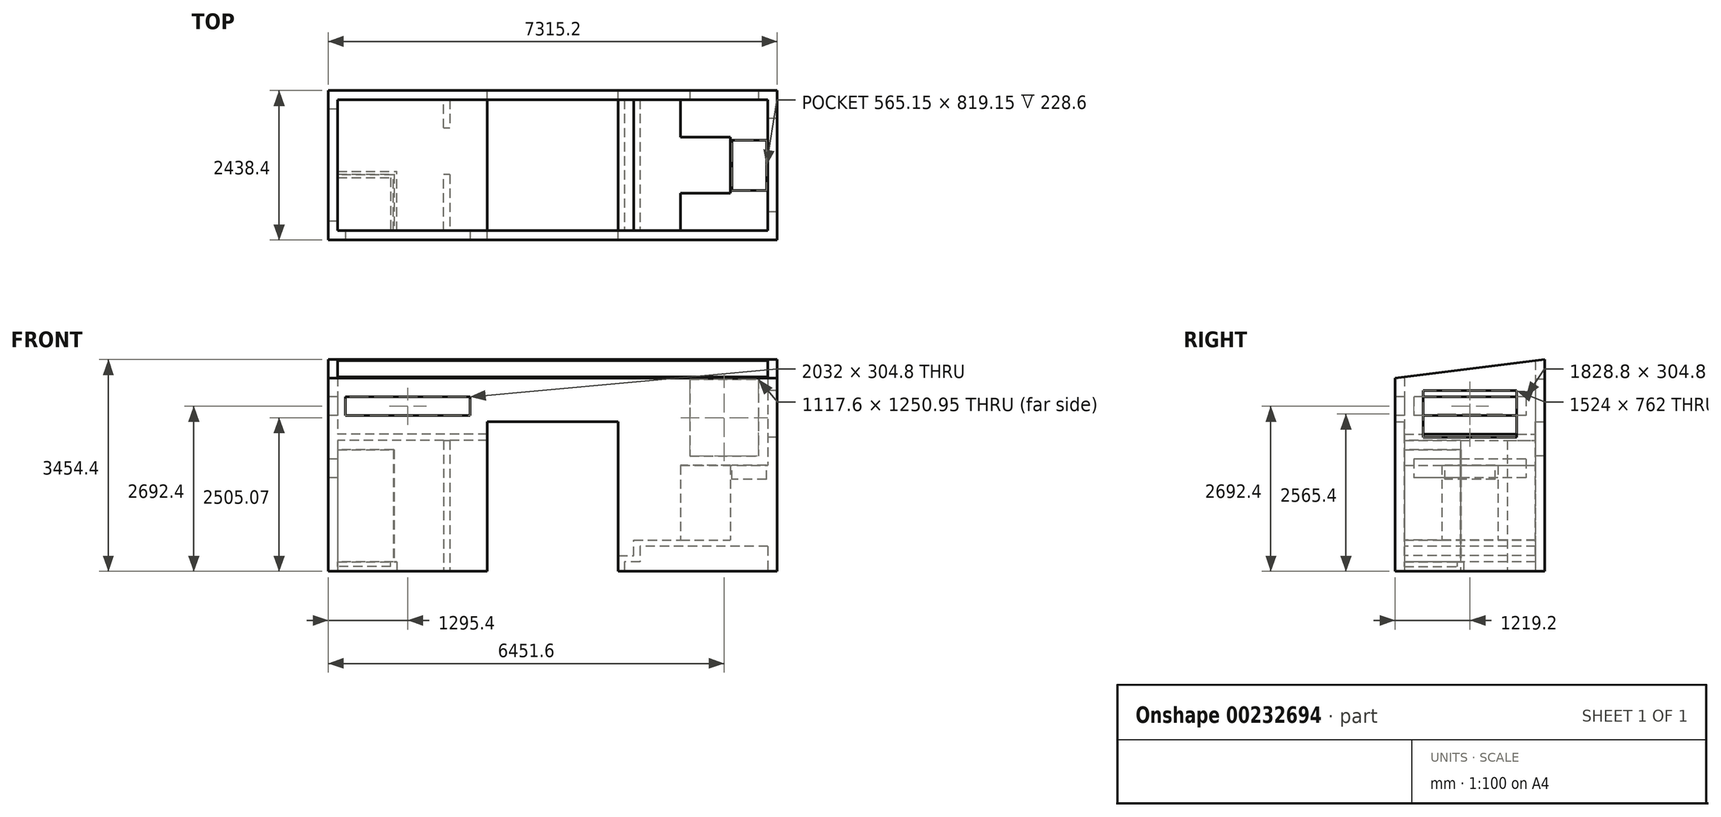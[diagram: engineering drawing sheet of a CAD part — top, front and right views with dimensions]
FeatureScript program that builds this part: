
annotation { "Feature Type Name" : "Feature", "Feature Type Description" : "" }
export const myFeature = defineFeature(function(context is Context, id is Id, definition is map)
    precondition{}
    {
        {
            var Q0;
            Q0=qCreatedBy(makeId("Top.planeOp"),FACE);
            var sketch = newSketch(context, id + "F0", { "sketchPlane" : qUnion([Q0])});
            skLineSegment(sketch, "E0.bottom", {"start": v(-3657.6, 1219.2) * mm, "end": v(3657.6, 1219.2) * mm});
            skLineSegment(sketch, "E0.top", {"start": v(-3657.6, -1219.2) * mm, "end": v(3657.6, -1219.2) * mm});
            skLineSegment(sketch, "E0.left", {"start": v(-3657.6, 1219.2) * mm, "end": v(-3657.6, -1219.2) * mm});
            skLineSegment(sketch, "E0.right", {"start": v(3657.6, 1219.2) * mm, "end": v(3657.6, -1219.2) * mm});
            skLineSegment(sketch, "E1", {"start": v(3657.6, 0) * mm, "end": v(-3657.6, 0) * mm, "construction": true});
            skLineSegment(sketch, "E2", {"start": v(0, 1219.2) * mm, "end": v(0, -1219.2) * mm, "construction": true});
            skSolve(sketch);
        }
        {
            var Q0;
            Q0 = qSketchRegion(id + "F0", true);
            extrude(context, id + "F1", {"entities" : qUnion([Q0]), "depth" : 4114.8 * mm - 660.4 * mm});
        }
        {
            var Q0;
            Q0=makeQuery(id+"F1.opExtrude","CAP_FACE",FACE,{"disambiguationData":[OSD([sQuery(id+"F0.wireOp",EDGE,"E0.bottom"),sQuery(id+"F0.wireOp",EDGE,"E0.top"),sQuery(id+"F0.wireOp",EDGE,"E0.left"),sQuery(id+"F0.wireOp",EDGE,"E0.right")])],"isStart":false});
            shell(context, id + "F2", {"entities" : qUnion([Q0]), "thickness" : 152.4 * mm});
        }
        {
            var Q0;
            Q0=makeQuery(id+"F1.opExtrude","SWEPT_FACE",FACE,{"disambiguationData":[OSD([sQuery(id+"F0.wireOp",EDGE,"E0.left")])]});
            var sketch = newSketch(context, id + "F3", { "sketchPlane" : qUnion([Q0])});
            skLineSegment(sketch, "E3", {"start": v(-1219.2, 3454.4) * mm, "end": v(1219.2, 3149.6) * mm});
            skLineSegment(sketch, "E4", {"start": v(1219.2, 3149.6) * mm, "end": v(1219.2, 3454.4) * mm});
            skLineSegment(sketch, "E5", {"start": v(1219.2, 3454.4) * mm, "end": v(-1219.2, 3454.4) * mm});
            skSolve(sketch);
        }
        {
            var Q0;
            Q0 = qSketchRegion(id + "F3", true);
            var Q1;
            Q1=makeQuery(id+"F1.opExtrude","SWEPT_FACE",FACE,{"disambiguationData":[OSD([sQuery(id+"F0.wireOp",EDGE,"E0.right")])]});
            extrude(context, id + "F4", {"entities" : qUnion([Q0]), "operationType" : NewBodyOperationType.REMOVE, "endBound" : BoundingType.UP_TO_SURFACE, "oppositeDirection" : true, "endBoundEntityFace" : qUnion([Q1]), "depth" : 25.4 * mm});
        }
        {
            var Q0;
            Q0=makeQuery(id+"F1.opExtrude","SWEPT_FACE",FACE,{"disambiguationData":[OSD([sQuery(id+"F0.wireOp",EDGE,"E0.bottom")])]});
            var sketch = newSketch(context, id + "F5", { "sketchPlane" : qUnion([Q0])});
            skLineSegment(sketch, "E6.bottom", {"start": v(-1066.8, 0) * mm, "end": v(1066.8, 0) * mm});
            skLineSegment(sketch, "E6.top", {"start": v(-1066.8, 2438.4) * mm, "end": v(1066.8, 2438.4) * mm});
            skLineSegment(sketch, "E6.left", {"start": v(-1066.8, 0) * mm, "end": v(-1066.8, 2438.4) * mm});
            skLineSegment(sketch, "E6.right", {"start": v(1066.8, 0) * mm, "end": v(1066.8, 2438.4) * mm});
            skLineSegment(sketch, "E7", {"start": v(0, 3454.4) * mm, "end": v(0, 0) * mm, "construction": true});
            skSolve(sketch);
        }
        {
            var Q0;
            Q0 = qSketchRegion(id + "F5", true);
            var Q1;
            Q1=makeQuery(id+"F1.opExtrude","SWEPT_FACE",FACE,{"disambiguationData":[OSD([sQuery(id+"F0.wireOp",EDGE,"E0.top")])]});
            extrude(context, id + "F6", {"entities" : qUnion([Q0]), "operationType" : NewBodyOperationType.REMOVE, "endBound" : BoundingType.UP_TO_SURFACE, "oppositeDirection" : true, "endBoundEntityFace" : qUnion([Q1]), "depth" : 25.4 * mm});
        }
        {
            var Q0;
            {var subQ0=sQuery(id+"F0.wireOp",EDGE,"E0.bottom");var subQ1=sQuery(id+"F0.wireOp",EDGE,"E0.top");var subQ2=sQuery(id+"F0.wireOp",EDGE,"E0.left");Q0=makeQuery(id+"F6.boolean.opBoolean","SPLIT",FACE,{"disambiguationData":[TD([makeQuery(id+"F2.opShell","OFFSET_FACE",FACE,{"disambiguationData":[OSD([subQ2])]})])],"derivedFrom":makeQuery(id+"F2.opShell","OFFSET_FACE",FACE,{"disambiguationData":[OSD([subQ0,subQ1,subQ2,sQuery(id+"F0.wireOp",EDGE,"E0.right")])]})});}
            var sketch = newSketch(context, id + "F7", { "sketchPlane" : qUnion([Q0])});
            skLineSegment(sketch, "E8.bottom", {"start": v(-3505.2, 1066.8) * mm, "end": v(3505.2, 1066.8) * mm});
            skLineSegment(sketch, "E8.top", {"start": v(-3505.2, -1066.8) * mm, "end": v(3505.2, -1066.8) * mm});
            skLineSegment(sketch, "E8.left", {"start": v(-3505.2, 1066.8) * mm, "end": v(-3505.2, -1066.8) * mm});
            skLineSegment(sketch, "E8.right", {"start": v(3505.2, 1066.8) * mm, "end": v(3505.2, -1066.8) * mm});
            skSolve(sketch);
        }
        {
            var Q0;
            Q0 = qSketchRegion(id + "F7", true);
            var Q1;
            {var subQ0=sQuery(id+"F0.wireOp",EDGE,"E0.bottom");var subQ1=sQuery(id+"F0.wireOp",EDGE,"E0.top");var subQ2=sQuery(id+"F0.wireOp",EDGE,"E0.left");Q1=makeQuery(id+"F6.boolean.opBoolean","SPLIT",FACE,{"disambiguationData":[TD([makeQuery(id+"F1.opExtrude","SWEPT_FACE",FACE,{"disambiguationData":[OSD([subQ2])]})])],"derivedFrom":makeQuery(id+"F1.opExtrude","CAP_FACE",FACE,{"disambiguationData":[OSD([subQ0,subQ1,subQ2,sQuery(id+"F0.wireOp",EDGE,"E0.right")])],"isStart":true})});}
            extrude(context, id + "F8", {"entities" : qUnion([Q0]), "operationType" : NewBodyOperationType.REMOVE, "endBound" : BoundingType.UP_TO_SURFACE, "oppositeDirection" : true, "endBoundEntityFace" : qUnion([Q1]), "depth" : 25.4 * mm});
        }
        {
            var Q0;
            Q0=makeQuery(id+"F8.boolean.opBoolean","MERGE",FACE,{"derivedFrom":[makeQuery(id+"F2.opShell","OFFSET_FACE",FACE,{"disambiguationData":[OSD([sQuery(id+"F0.wireOp",EDGE,"E0.left")])]}),makeQuery(id+"F8.opExtrude","SWEPT_FACE",FACE,{"disambiguationData":[OSD([sQuery(id+"F7.wireOp",EDGE,"E8.left")])]})]});
            var sketch = newSketch(context, id + "F9", { "sketchPlane" : qUnion([Q0])});
            skLineSegment(sketch, "E9.bottom", {"start": v(-1066.8, 2235.2) * mm, "end": v(1066.8, 2235.2) * mm});
            skLineSegment(sketch, "E9.top", {"start": v(-1066.8, 2133.6) * mm, "end": v(1066.8, 2133.6) * mm});
            skLineSegment(sketch, "E9.left", {"start": v(-1066.8, 2235.2) * mm, "end": v(-1066.8, 2133.6) * mm});
            skLineSegment(sketch, "E9.right", {"start": v(1066.8, 2235.2) * mm, "end": v(1066.8, 2133.6) * mm});
            skSolve(sketch);
        }
        {
            var Q0;
            Q0 = qSketchRegion(id + "F9", true);
            extrude(context, id + "F10", {"entities" : qUnion([Q0]), "operationType" : NewBodyOperationType.ADD, "depth" : 2438.4 * mm});
        }
        {
            var Q0;
            {var subQ0=sQuery(id+"F0.wireOp",EDGE,"E0.top");var subQ1=makeQuery(id+"F2.opShell","OFFSET_FACE",FACE,{"disambiguationData":[OSD([subQ0])]});var subQ4=sQuery(id+"F0.wireOp",EDGE,"E0.right");Q0=makeQuery(id+"F10.boolean.opBoolean","SPLIT",FACE,{"disambiguationData":[TD([makeQuery(id+"F2.opShell","OFFSET_FACE",FACE,{"disambiguationData":[OSD([subQ4])]})])],"derivedFrom":makeQuery(id+"F8.boolean.opBoolean","MERGE",FACE,{"derivedFrom":[subQ1,makeQuery(id+"F8.opExtrude","SWEPT_FACE",FACE,{"disambiguationData":[OSD([sQuery(id+"F7.wireOp",EDGE,"E8.top")])]})]})});}
            var sketch = newSketch(context, id + "F11", { "sketchPlane" : qUnion([Q0])});
            skLineSegment(sketch, "E10", {"start": v(-1066.8, 0) * mm, "end": v(-1066.8, 254) * mm});
            skLineSegment(sketch, "E11", {"start": v(-1066.8, 254) * mm, "end": v(-1320.8, 254) * mm});
            skLineSegment(sketch, "E12", {"start": v(-1320.8, 254) * mm, "end": v(-1320.8, 508) * mm});
            skLineSegment(sketch, "E13", {"start": v(-1320.8, 508) * mm, "end": v(-3657.6, 508) * mm});
            skLineSegment(sketch, "E14", {"start": v(-3657.6, 508) * mm, "end": v(-3657.6, 406.4) * mm});
            skLineSegment(sketch, "E15", {"start": v(-3657.6, 406.4) * mm, "end": v(-1422.4, 406.4) * mm});
            skLineSegment(sketch, "E16", {"start": v(-1422.4, 406.4) * mm, "end": v(-1422.4, 152.4) * mm});
            skLineSegment(sketch, "E17", {"start": v(-1422.4, 152.4) * mm, "end": v(-1168.4, 152.4) * mm});
            skLineSegment(sketch, "E18", {"start": v(-1168.4, 152.4) * mm, "end": v(-1168.4, 0) * mm});
            skLineSegment(sketch, "E19", {"start": v(-1168.4, 0) * mm, "end": v(-1066.8, 0) * mm});
            skSolve(sketch);
        }
        {
            var Q0;
            Q0 = qSketchRegion(id + "F11", true);
            var Q1;
            {var subQ1=sQuery(id+"F0.wireOp",EDGE,"E0.right");var subQ2=sQuery(id+"F0.wireOp",EDGE,"E0.bottom");var subQ3=makeQuery(id+"F2.opShell","OFFSET_FACE",FACE,{"disambiguationData":[OSD([subQ2])]});Q1=makeQuery(id+"F10.boolean.opBoolean","SPLIT",FACE,{"disambiguationData":[TD([makeQuery(id+"F2.opShell","OFFSET_FACE",FACE,{"disambiguationData":[OSD([subQ1])]})])],"derivedFrom":makeQuery(id+"F8.boolean.opBoolean","MERGE",FACE,{"derivedFrom":[subQ3,makeQuery(id+"F8.opExtrude","SWEPT_FACE",FACE,{"disambiguationData":[OSD([sQuery(id+"F7.wireOp",EDGE,"E8.bottom")])]})]})});}
            extrude(context, id + "F12", {"entities" : qUnion([Q0]), "operationType" : NewBodyOperationType.ADD, "endBound" : BoundingType.UP_TO_SURFACE, "endBoundEntityFace" : qUnion([Q1]), "depth" : 25.4 * mm});
        }
        {
            var Q0;
            {var subQ4=sQuery(id+"F0.wireOp",EDGE,"E0.right");var subQ5=makeQuery(id+"F2.opShell","OFFSET_FACE",FACE,{"disambiguationData":[OSD([subQ4])]});var subQ6=sQuery(id+"F0.wireOp",EDGE,"E0.left");var subQ7=makeQuery(id+"F2.opShell","OFFSET_FACE",FACE,{"disambiguationData":[OSD([subQ6])]});var subQ10=sQuery(id+"F0.wireOp",EDGE,"E0.bottom");var subQ11=makeQuery(id+"F2.opShell","OFFSET_FACE",FACE,{"disambiguationData":[OSD([subQ10])]});Q0=makeQuery(id+"F12.boolean.opBoolean","SPLIT",FACE,{"disambiguationData":[TD([subQ7])],"derivedFrom":makeQuery(id+"F10.boolean.opBoolean","SPLIT",FACE,{"disambiguationData":[TD([subQ5])],"derivedFrom":makeQuery(id+"F8.boolean.opBoolean","MERGE",FACE,{"derivedFrom":[subQ11,makeQuery(id+"F8.opExtrude","SWEPT_FACE",FACE,{"disambiguationData":[OSD([sQuery(id+"F7.wireOp",EDGE,"E8.bottom")])]})]})})});}
            var sketch = newSketch(context, id + "F13", { "sketchPlane" : qUnion([Q0])});
            skLineSegment(sketch, "E20.bottom", {"start": v(2235.2, 3130.55) * mm, "end": v(3352.8, 3130.55) * mm});
            skLineSegment(sketch, "E20.top", {"start": v(2235.2, 1879.6) * mm, "end": v(3352.8, 1879.6) * mm});
            skLineSegment(sketch, "E20.left", {"start": v(2235.2, 3130.55) * mm, "end": v(2235.2, 1879.6) * mm});
            skLineSegment(sketch, "E20.right", {"start": v(3352.8, 3130.55) * mm, "end": v(3352.8, 1879.6) * mm});
            skSolve(sketch);
        }
        {
            var Q0;
            Q0=makeQuery(id+"F13.imprint","IMPRINT",FACE,{"disambiguationData":[TD([[makeQuery(id+"F13.imprint","IMPRINT",EDGE,{"derivedFrom":sQuery(id+"F13.wireOp",EDGE,"E20.bottom")}),-1.0]])]});
            var Q1;
            Q1=makeQuery(id+"F1.opExtrude","SWEPT_FACE",FACE,{"disambiguationData":[OSD([sQuery(id+"F0.wireOp",EDGE,"E0.bottom")])]});
            extrude(context, id + "F14", {"entities" : qUnion([Q0]), "operationType" : NewBodyOperationType.REMOVE, "endBound" : BoundingType.UP_TO_SURFACE, "oppositeDirection" : true, "endBoundEntityFace" : qUnion([Q1]), "depth" : 25.4 * mm});
        }
        {
            var Q0;
            Q0=makeQuery(id+"F12.opExtrude","SWEPT_FACE",FACE,{"disambiguationData":[OSD([sQuery(id+"F11.wireOp",EDGE,"E13")])]});
            var sketch = newSketch(context, id + "F15", { "sketchPlane" : qUnion([Q0])});
            skLineSegment(sketch, "E21", {"start": v(2082.8, 1066.8) * mm, "end": v(3505.2, 1066.8) * mm});
            skLineSegment(sketch, "E22", {"start": v(3505.2, 1066.8) * mm, "end": v(3505.2, -1066.8) * mm});
            skLineSegment(sketch, "E23", {"start": v(3505.2, -1066.8) * mm, "end": v(2082.8, -1066.8) * mm});
            skLineSegment(sketch, "E24", {"start": v(2082.8, -1066.8) * mm, "end": v(2082.8, -457.2) * mm});
            skLineSegment(sketch, "E25", {"start": v(2082.8, -457.2) * mm, "end": v(2895.6, -457.2) * mm});
            skLineSegment(sketch, "E26", {"start": v(2895.6, -457.2) * mm, "end": v(2895.6, 457.2) * mm});
            skLineSegment(sketch, "E27", {"start": v(2895.6, 457.2) * mm, "end": v(2082.8, 457.2) * mm});
            skLineSegment(sketch, "E28", {"start": v(2082.8, 457.2) * mm, "end": v(2082.8, 1066.8) * mm});
            skSolve(sketch);
        }
        {
            var Q0;
            Q0 = qSketchRegion(id + "F15", true);
            extrude(context, id + "F16", {"entities" : qUnion([Q0]), "operationType" : NewBodyOperationType.ADD, "depth" : 1219.2 * mm});
        }
        {
            var Q0;
            Q0=makeQuery(id+"F12.boolean.opBoolean","SPLIT",FACE,{"disambiguationData":[TD([makeQuery(id+"F4.boolean.opBoolean","COPY",FACE,{"derivedFrom":makeQuery(id+"F4.opExtrude","SWEPT_FACE",FACE,{"disambiguationData":[OSD([sQuery(id+"F3.wireOp",EDGE,"E3")])]})})])],"derivedFrom":makeQuery(id+"F8.boolean.opBoolean","MERGE",FACE,{"derivedFrom":[makeQuery(id+"F2.opShell","OFFSET_FACE",FACE,{"disambiguationData":[OSD([sQuery(id+"F0.wireOp",EDGE,"E0.right")])]}),makeQuery(id+"F8.opExtrude","SWEPT_FACE",FACE,{"disambiguationData":[OSD([sQuery(id+"F7.wireOp",EDGE,"E8.right")])]})]})});
            var sketch = newSketch(context, id + "F17", { "sketchPlane" : qUnion([Q0])});
            skLineSegment(sketch, "E29.bottom", {"start": v(-762, 2946.4) * mm, "end": v(762, 2946.4) * mm});
            skLineSegment(sketch, "E29.top", {"start": v(-762, 2184.4) * mm, "end": v(762, 2184.4) * mm});
            skLineSegment(sketch, "E29.left", {"start": v(-762, 2946.4) * mm, "end": v(-762, 2184.4) * mm});
            skLineSegment(sketch, "E29.right", {"start": v(762, 2946.4) * mm, "end": v(762, 2184.4) * mm});
            skLineSegment(sketch, "E30", {"start": v(0, 1727.2) * mm, "end": v(0, 2946.4) * mm, "construction": true});
            skSolve(sketch);
        }
        {
            var Q0;
            Q0 = qSketchRegion(id + "F17", true);
            var Q1;
            Q1=makeQuery(id+"F1.opExtrude","SWEPT_FACE",FACE,{"disambiguationData":[OSD([sQuery(id+"F0.wireOp",EDGE,"E0.right")])]});
            extrude(context, id + "F18", {"entities" : qUnion([Q0]), "operationType" : NewBodyOperationType.REMOVE, "endBound" : BoundingType.UP_TO_SURFACE, "oppositeDirection" : true, "endBoundEntityFace" : qUnion([Q1]), "depth" : 25.4 * mm});
        }
        {
            var Q0;
            Q0=makeQuery(id+"F16.opExtrude","CAP_FACE",FACE,{"disambiguationData":[OSD([sQuery(id+"F15.wireOp",EDGE,"E21"),sQuery(id+"F15.wireOp",EDGE,"E22"),sQuery(id+"F15.wireOp",EDGE,"E23"),sQuery(id+"F15.wireOp",EDGE,"E24"),sQuery(id+"F15.wireOp",EDGE,"E25"),sQuery(id+"F15.wireOp",EDGE,"E26"),sQuery(id+"F15.wireOp",EDGE,"E27"),sQuery(id+"F15.wireOp",EDGE,"E28")])],"isStart":false});
            var sketch = newSketch(context, id + "F19", { "sketchPlane" : qUnion([Q0])});
            skLineSegment(sketch, "E31.bottom", {"start": v(3482.98, 409.58) * mm, "end": v(2917.83, 409.58) * mm});
            skLineSegment(sketch, "E31.top", {"start": v(3482.98, -409.57) * mm, "end": v(2917.83, -409.57) * mm});
            skLineSegment(sketch, "E31.left", {"start": v(3482.98, 409.57) * mm, "end": v(3482.98, -409.57) * mm});
            skLineSegment(sketch, "E31.right", {"start": v(2917.83, 409.57) * mm, "end": v(2917.83, -409.57) * mm});
            skLineSegment(sketch, "E32", {"start": v(3505.2, 0) * mm, "end": v(2895.6, 0) * mm, "construction": true});
            skLineSegment(sketch, "E33", {"start": v(3200.4, 1066.8) * mm, "end": v(3200.4, -1066.8) * mm, "construction": true});
            skPoint(sketch, "E34", {"position": v(3200.4, 409.57) * mm});
            skPoint(sketch, "E35", {"position": v(3200.4, -409.57) * mm});
            skPoint(sketch, "E36", {"position": v(3482.98, 0) * mm});
            skPoint(sketch, "E37", {"position": v(2917.83, 0) * mm});
            skPoint(sketch, "E38", {"position": v(3200.4, 0) * mm});
            skSolve(sketch);
        }
        {
            var Q0;
            Q0 = qSketchRegion(id + "F19", true);
            extrude(context, id + "F20", {"entities" : qUnion([Q0]), "operationType" : NewBodyOperationType.REMOVE, "oppositeDirection" : true, "depth" : 228.6 * mm});
        }
        {
            var Q0;
            Q0=makeQuery(id+"F10.opExtrude","SWEPT_FACE",FACE,{"disambiguationData":[OSD([sQuery(id+"F9.wireOp",EDGE,"E9.bottom")])]});
            var sketch = newSketch(context, id + "F21", { "sketchPlane" : qUnion([Q0])});
            skLineSegment(sketch, "E39.bottom", {"start": v(-3386.05, -1025.69) * mm, "end": v(-1862.05, -1025.69) * mm});
            skLineSegment(sketch, "E39.top", {"start": v(-3386.05, 1006.31) * mm, "end": v(-1862.05, 1006.31) * mm});
            skLineSegment(sketch, "E39.left", {"start": v(-3386.05, -1025.69) * mm, "end": v(-3386.05, 1006.31) * mm});
            skLineSegment(sketch, "E39.right", {"start": v(-1862.05, -1025.69) * mm, "end": v(-1862.05, 1006.31) * mm});
            skSolve(sketch);
        }
        {
            var Q0;
            Q0=makeQuery(id+"F1.opExtrude","SWEPT_FACE",FACE,{"disambiguationData":[OSD([sQuery(id+"F0.wireOp",EDGE,"E0.left")])]});
            var sketch = newSketch(context, id + "F22", { "sketchPlane" : qUnion([Q0])});
            skLineSegment(sketch, "E40.bottom", {"start": v(-914.4, 2844.8) * mm, "end": v(914.4, 2844.8) * mm});
            skLineSegment(sketch, "E40.top", {"start": v(-914.4, 2540) * mm, "end": v(914.4, 2540) * mm});
            skLineSegment(sketch, "E40.left", {"start": v(-914.4, 2844.8) * mm, "end": v(-914.4, 2540) * mm});
            skLineSegment(sketch, "E40.right", {"start": v(914.4, 2844.8) * mm, "end": v(914.4, 2540) * mm});
            skLineSegment(sketch, "E41.bottom", {"start": v(-913.36, 1828.8) * mm, "end": v(915.44, 1828.8) * mm});
            skLineSegment(sketch, "E41.top", {"start": v(-913.36, 1524) * mm, "end": v(915.44, 1524) * mm});
            skLineSegment(sketch, "E41.left", {"start": v(-913.36, 1828.8) * mm, "end": v(-913.36, 1524) * mm});
            skLineSegment(sketch, "E41.right", {"start": v(915.44, 1828.8) * mm, "end": v(915.44, 1524) * mm});
            skSolve(sketch);
        }
        {
            var Q0;
            Q0 = qSketchRegion(id + "F22", true);
            var Q1;
            Q1=makeQuery(id+"F10.boolean.opBoolean","SPLIT",FACE,{"disambiguationData":[TD([makeQuery(id+"F4.boolean.opBoolean","COPY",FACE,{"derivedFrom":makeQuery(id+"F4.opExtrude","SWEPT_FACE",FACE,{"disambiguationData":[OSD([sQuery(id+"F3.wireOp",EDGE,"E3")])]})})])],"derivedFrom":makeQuery(id+"F8.boolean.opBoolean","MERGE",FACE,{"derivedFrom":[makeQuery(id+"F2.opShell","OFFSET_FACE",FACE,{"disambiguationData":[OSD([sQuery(id+"F0.wireOp",EDGE,"E0.left")])]}),makeQuery(id+"F8.opExtrude","SWEPT_FACE",FACE,{"disambiguationData":[OSD([sQuery(id+"F7.wireOp",EDGE,"E8.left")])]})]})});
            extrude(context, id + "F23", {"entities" : qUnion([Q0]), "operationType" : NewBodyOperationType.REMOVE, "endBound" : BoundingType.UP_TO_SURFACE, "oppositeDirection" : true, "endBoundEntityFace" : qUnion([Q1]), "depth" : 25.4 * mm});
        }
        {
            var Q0;
            {var subQ0=sQuery(id+"F0.wireOp",EDGE,"E0.bottom");var subQ1=sQuery(id+"F0.wireOp",EDGE,"E0.top");var subQ2=sQuery(id+"F0.wireOp",EDGE,"E0.left");Q0=makeQuery(id+"F6.boolean.opBoolean","SPLIT",FACE,{"disambiguationData":[TD([makeQuery(id+"F1.opExtrude","SWEPT_FACE",FACE,{"disambiguationData":[OSD([subQ2])]})])],"derivedFrom":makeQuery(id+"F1.opExtrude","CAP_FACE",FACE,{"disambiguationData":[OSD([subQ0,subQ1,subQ2,sQuery(id+"F0.wireOp",EDGE,"E0.right")])],"isStart":true})});}
            var sketch = newSketch(context, id + "F24", { "sketchPlane" : qUnion([Q0])});
            skLineSegment(sketch, "E42", {"start": v(-1778, 1066.8) * mm, "end": v(-1778, 152.4) * mm});
            skLineSegment(sketch, "E43", {"start": v(-1676.4, 152.4) * mm, "end": v(-1778, 152.4) * mm});
            skLineSegment(sketch, "E44", {"start": v(-1676.4, 152.4) * mm, "end": v(-1676.4, 1066.8) * mm});
            skLineSegment(sketch, "E45", {"start": v(-1778, 1066.8) * mm, "end": v(-1676.4, 1066.8) * mm});
            skLineSegment(sketch, "E46", {"start": v(-1778, -609.6) * mm, "end": v(-1778, -1066.8) * mm});
            skLineSegment(sketch, "E47", {"start": v(-1676.4, -1066.8) * mm, "end": v(-1778, -1066.8) * mm});
            skLineSegment(sketch, "E48", {"start": v(-1676.4, -1066.8) * mm, "end": v(-1676.4, -609.6) * mm});
            skLineSegment(sketch, "E49", {"start": v(-1778, -609.6) * mm, "end": v(-1676.4, -609.6) * mm});
            skSolve(sketch);
        }
        {
            var Q0;
            Q0 = qSketchRegion(id + "F24", true);
            var Q1;
            Q1=makeQuery(id+"F10.opExtrude","SWEPT_FACE",FACE,{"disambiguationData":[OSD([sQuery(id+"F9.wireOp",EDGE,"E9.top")])]});
            extrude(context, id + "F25", {"entities" : qUnion([Q0]), "operationType" : NewBodyOperationType.ADD, "endBound" : BoundingType.UP_TO_SURFACE, "oppositeDirection" : true, "endBoundEntityFace" : qUnion([Q1]), "depth" : 25.4 * mm});
        }
        {
            var Q0;
            {var subQ0=sQuery(id+"F0.wireOp",EDGE,"E0.bottom");var subQ1=sQuery(id+"F0.wireOp",EDGE,"E0.top");var subQ2=sQuery(id+"F0.wireOp",EDGE,"E0.left");Q0=makeQuery(id+"F25.boolean.opBoolean","MERGE",FACE,{"derivedFrom":[makeQuery(id+"F6.boolean.opBoolean","SPLIT",FACE,{"disambiguationData":[TD([makeQuery(id+"F1.opExtrude","SWEPT_FACE",FACE,{"disambiguationData":[OSD([subQ2])]})])],"derivedFrom":makeQuery(id+"F1.opExtrude","CAP_FACE",FACE,{"disambiguationData":[OSD([subQ0,subQ1,subQ2,sQuery(id+"F0.wireOp",EDGE,"E0.right")])],"isStart":true})}),makeQuery(id+"F25.opExtrude","CAP_FACE",FACE,{"disambiguationData":[OSD([sQuery(id+"F24.wireOp",EDGE,"E42"),sQuery(id+"F24.wireOp",EDGE,"E43"),sQuery(id+"F24.wireOp",EDGE,"E44"),sQuery(id+"F24.wireOp",EDGE,"E45")])],"isStart":true}),makeQuery(id+"F25.opExtrude","CAP_FACE",FACE,{"disambiguationData":[OSD([sQuery(id+"F24.wireOp",EDGE,"E46"),sQuery(id+"F24.wireOp",EDGE,"E47"),sQuery(id+"F24.wireOp",EDGE,"E48"),sQuery(id+"F24.wireOp",EDGE,"E49")])],"isStart":true})]});}
            var sketch = newSketch(context, id + "F26", { "sketchPlane" : qUnion([Q0])});
            skLineSegment(sketch, "E50.bottom", {"start": v(-3505.2, 1066.8) * mm, "end": v(-2540, 1066.8) * mm});
            skLineSegment(sketch, "E50.top", {"start": v(-3505.2, 101.6) * mm, "end": v(-2540, 101.6) * mm});
            skLineSegment(sketch, "E50.left", {"start": v(-3505.2, 1066.8) * mm, "end": v(-3505.2, 101.6) * mm});
            skLineSegment(sketch, "E50.right", {"start": v(-2540, 1066.8) * mm, "end": v(-2540, 101.6) * mm});
            skSolve(sketch);
        }
        {
            var Q0;
            Q0 = qSketchRegion(id + "F26", true);
            extrude(context, id + "F27", {"entities" : qUnion([Q0]), "operationType" : NewBodyOperationType.ADD, "oppositeDirection" : true, "depth" : 152.4 * mm});
        }
        {
            var Q0;
            Q0=makeQuery(id+"F27.opExtrude","CAP_FACE",FACE,{"disambiguationData":[OSD([sQuery(id+"F26.wireOp",EDGE,"E50.bottom"),sQuery(id+"F26.wireOp",EDGE,"E50.top"),sQuery(id+"F26.wireOp",EDGE,"E50.left"),sQuery(id+"F26.wireOp",EDGE,"E50.right")])],"isStart":false});
            var sketch = newSketch(context, id + "F28", { "sketchPlane" : qUnion([Q0])});
            skLineSegment(sketch, "E51.bottom", {"start": v(-3505.2, -203.2) * mm, "end": v(-2641.6, -203.2) * mm});
            skLineSegment(sketch, "E51.top", {"start": v(-3505.2, -1066.8) * mm, "end": v(-2641.6, -1066.8) * mm});
            skLineSegment(sketch, "E51.left", {"start": v(-3505.2, -203.2) * mm, "end": v(-3505.2, -1066.8) * mm});
            skLineSegment(sketch, "E51.right", {"start": v(-2641.6, -203.2) * mm, "end": v(-2641.6, -1066.8) * mm});
            skSolve(sketch);
        }
        {
            var Q0;
            Q0 = qSketchRegion(id + "F28", true);
            extrude(context, id + "F29", {"entities" : qUnion([Q0]), "operationType" : NewBodyOperationType.REMOVE, "oppositeDirection" : true, "depth" : 76.2 * mm});
        }
        {
            var Q0;
            Q0=makeQuery(id+"F27.opExtrude","CAP_FACE",FACE,{"disambiguationData":[OSD([sQuery(id+"F26.wireOp",EDGE,"E50.bottom"),sQuery(id+"F26.wireOp",EDGE,"E50.top"),sQuery(id+"F26.wireOp",EDGE,"E50.left"),sQuery(id+"F26.wireOp",EDGE,"E50.right")])],"isStart":false});
            var sketch = newSketch(context, id + "F30", { "sketchPlane" : qUnion([Q0])});
            skLineSegment(sketch, "E52", {"start": v(-3505.2, -146.05) * mm, "end": v(-2584.45, -146.05) * mm});
            skLineSegment(sketch, "E53", {"start": v(-2584.45, -146.05) * mm, "end": v(-2584.45, -1066.8) * mm});
            skLineSegment(sketch, "E54", {"start": v(-2584.45, -1066.8) * mm, "end": v(-2597.15, -1066.8) * mm});
            skLineSegment(sketch, "E55", {"start": v(-2597.15, -1066.8) * mm, "end": v(-2597.15, -158.75) * mm});
            skLineSegment(sketch, "E56", {"start": v(-2597.15, -158.75) * mm, "end": v(-3505.2, -158.75) * mm});
            skLineSegment(sketch, "E57", {"start": v(-3505.2, -146.05) * mm, "end": v(-3505.2, -158.75) * mm});
            skLineSegment(sketch, "E58", {"start": v(-2590.8, -1066.8) * mm, "end": v(-2590.8, -101.6) * mm, "construction": true});
            skLineSegment(sketch, "E59", {"start": v(-3505.2, -152.4) * mm, "end": v(-2540, -152.4) * mm, "construction": true});
            skSolve(sketch);
        }
        {
            var Q0;
            Q0 = qSketchRegion(id + "F30", true);
            extrude(context, id + "F31", {"entities" : qUnion([Q0]), "operationType" : NewBodyOperationType.ADD, "depth" : 1828.8 * mm});
        }
        {
            var Q0;
            Q0=makeQuery(id+"F1.opExtrude","SWEPT_FACE",FACE,{"disambiguationData":[OSD([sQuery(id+"F0.wireOp",EDGE,"E0.top")])]});
            var sketch = newSketch(context, id + "F32", { "sketchPlane" : qUnion([Q0])});
            skLineSegment(sketch, "E60.bottom", {"start": v(-3378.2, 2844.8) * mm, "end": v(-1346.2, 2844.8) * mm});
            skLineSegment(sketch, "E60.top", {"start": v(-3378.2, 2540) * mm, "end": v(-1346.2, 2540) * mm});
            skLineSegment(sketch, "E60.left", {"start": v(-3378.2, 2844.8) * mm, "end": v(-3378.2, 2540) * mm});
            skLineSegment(sketch, "E60.right", {"start": v(-1346.2, 2844.8) * mm, "end": v(-1346.2, 2540) * mm});
            skLineSegment(sketch, "E61", {"start": v(-2362.2, 0) * mm, "end": v(-2362.2, 3149.6) * mm, "construction": true});
            skPoint(sketch, "E62", {"position": v(-2362.2, 2844.8) * mm});
            skSolve(sketch);
        }
        {
            var Q0;
            Q0 = qSketchRegion(id + "F32", true);
            var Q1;
            {var subQ2=sQuery(id+"F0.wireOp",EDGE,"E0.top");var subQ3=makeQuery(id+"F2.opShell","OFFSET_FACE",FACE,{"disambiguationData":[OSD([subQ2])]});var subQ9=sQuery(id+"F0.wireOp",EDGE,"E0.right");var subQ10=makeQuery(id+"F2.opShell","OFFSET_FACE",FACE,{"disambiguationData":[OSD([subQ9])]});var subQ11=sQuery(id+"F0.wireOp",EDGE,"E0.left");var subQ12=makeQuery(id+"F2.opShell","OFFSET_FACE",FACE,{"disambiguationData":[OSD([subQ11])]});Q1=makeQuery(id+"F12.boolean.opBoolean","SPLIT",FACE,{"disambiguationData":[TD([subQ12])],"derivedFrom":makeQuery(id+"F10.boolean.opBoolean","SPLIT",FACE,{"disambiguationData":[TD([subQ10])],"derivedFrom":makeQuery(id+"F8.boolean.opBoolean","MERGE",FACE,{"derivedFrom":[subQ3,makeQuery(id+"F8.opExtrude","SWEPT_FACE",FACE,{"disambiguationData":[OSD([sQuery(id+"F7.wireOp",EDGE,"E8.top")])]})]})})});}
            extrude(context, id + "F33", {"entities" : qUnion([Q0]), "operationType" : NewBodyOperationType.REMOVE, "endBound" : BoundingType.UP_TO_SURFACE, "oppositeDirection" : true, "endBoundEntityFace" : qUnion([Q1]), "depth" : 25.4 * mm});
        }
    });
